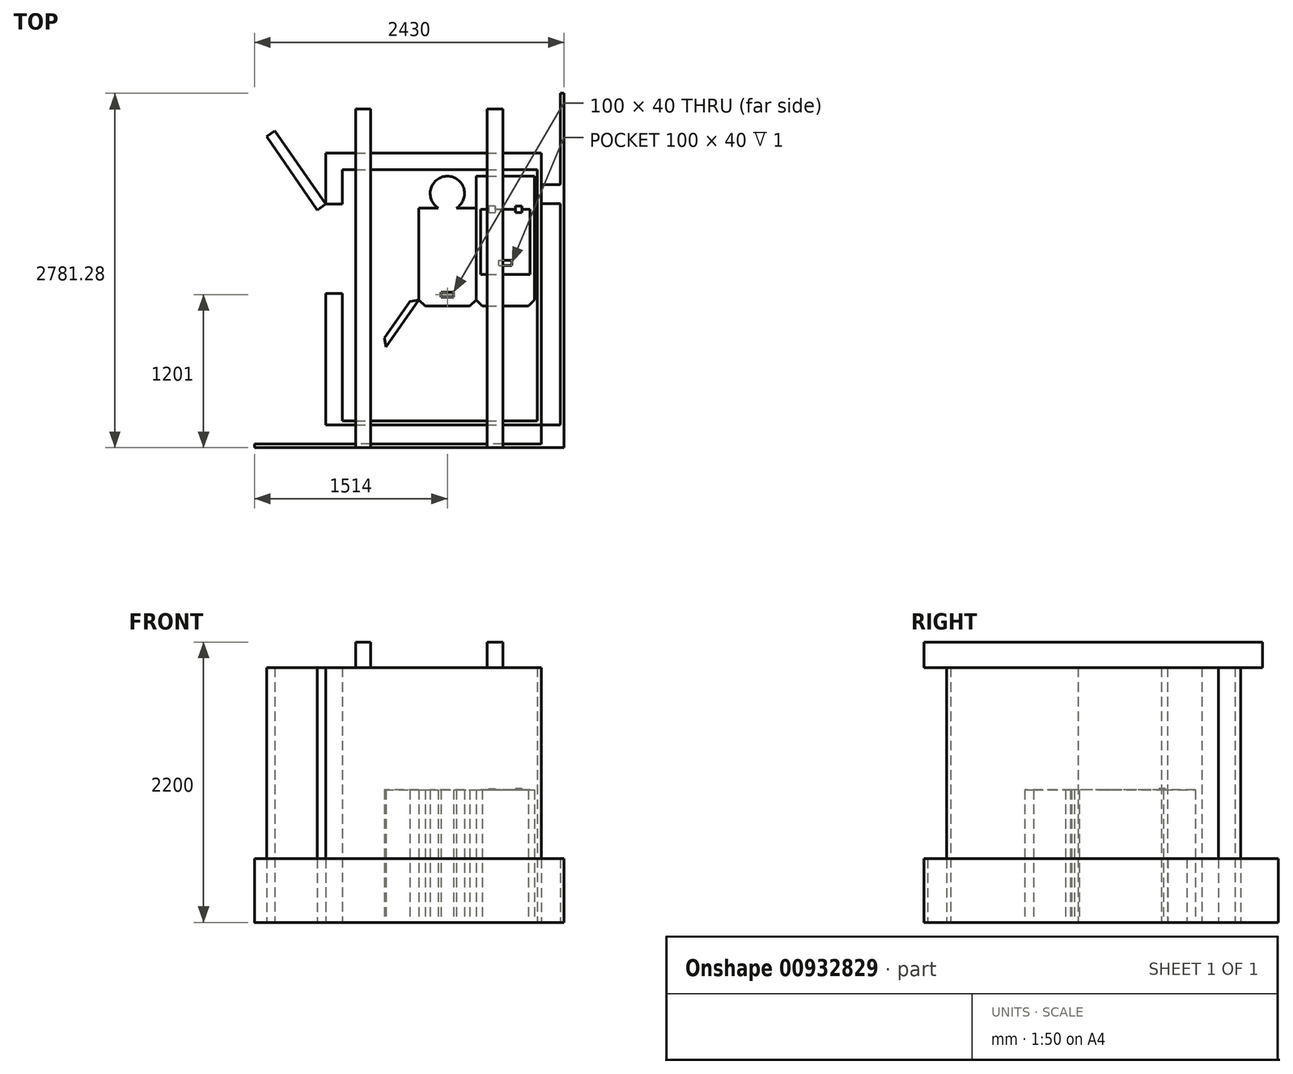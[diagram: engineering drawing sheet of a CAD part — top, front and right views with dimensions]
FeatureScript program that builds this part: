
annotation { "Feature Type Name" : "Feature", "Feature Type Description" : "" }
export const myFeature = defineFeature(function(context is Context, id is Id, definition is map)
    precondition{}
    {
        {
            var Q0;
            Q0=qCreatedBy(makeId("Top.planeOp"),FACE);
            var sketch = newSketch(context, id + "F0", { "sketchPlane" : qUnion([Q0])});
            skLineSegment(sketch, "E0", {"start": v(-30, 2781.28) * mm, "end": v(-30, 30) * mm});
            skLineSegment(sketch, "E1", {"start": v(-30, 30) * mm, "end": v(-2430, 30) * mm});
            skLineSegment(sketch, "E2", {"start": v(-2430, 30) * mm, "end": v(-2430, 0) * mm});
            skLineSegment(sketch, "E3", {"start": v(-2430, 0) * mm, "end": v(0, 0) * mm});
            skLineSegment(sketch, "E4", {"start": v(0, 0) * mm, "end": v(0, 2781.28) * mm});
            skLineSegment(sketch, "E5", {"start": v(0, 2781.28) * mm, "end": v(-30, 2781.28) * mm});
            skLineSegment(sketch, "E6", {"start": v(-2460, -1250) * mm, "end": v(-2460, 0) * mm});
            skLineSegment(sketch, "E7", {"start": v(-2460, 0) * mm, "end": v(-2430, 0) * mm});
            skLineSegment(sketch, "E8", {"start": v(-2430, 0) * mm, "end": v(-2430, -1250) * mm});
            skLineSegment(sketch, "E9", {"start": v(-2430, -1250) * mm, "end": v(-2460, -1250) * mm});
            skArc(sketch, "E10", {"start": v(-2460, -1250) * mm, "mid": v(-3343.88, -883.88) * mm, "end": v(-3710, 0) * mm, "construction": true});
            skLineSegment(sketch, "E11.bottom", {"start": v(-1872, 180) * mm, "end": v(-180, 180) * mm});
            skLineSegment(sketch, "E11.top", {"start": v(-1872, 2312) * mm, "end": v(-180, 2312) * mm});
            skLineSegment(sketch, "E11.right", {"start": v(-180, 180) * mm, "end": v(-180, 2312) * mm});
            skLineSegment(sketch, "E12.bottom", {"start": v(-1741, 2181) * mm, "end": v(-211, 2181) * mm});
            skLineSegment(sketch, "E12.top", {"start": v(-1741, 211) * mm, "end": v(-211, 211) * mm});
            skLineSegment(sketch, "E12.left", {"start": v(-1741, 2181) * mm, "end": v(-1741, 1911) * mm});
            skLineSegment(sketch, "E12.right", {"start": v(-211, 2181) * mm, "end": v(-211, 211) * mm});
            skLineSegment(sketch, "E13", {"start": v(-1872, 1911) * mm, "end": v(-1741, 1911) * mm});
            skLineSegment(sketch, "E14.trimOffspring", {"start": v(-1872, 1911) * mm, "end": v(-1872, 2312) * mm});
            skLineSegment(sketch, "E15", {"start": v(-211, 2312) * mm, "end": v(-211, 2181) * mm});
            skLineSegment(sketch, "E16", {"start": v(-180, 2181) * mm, "end": v(-211, 2181) * mm});
            skLineSegment(sketch, "E17", {"start": v(-180, 211) * mm, "end": v(-211, 211) * mm});
            skLineSegment(sketch, "E18", {"start": v(-211, 180) * mm, "end": v(-211, 211) * mm});
            skLineSegment(sketch, "E19", {"start": v(-1741, 211) * mm, "end": v(-1741, 1211) * mm});
            skLineSegment(sketch, "E20", {"start": v(-1741, 1211) * mm, "end": v(-1872, 1211) * mm});
            skLineSegment(sketch, "E21", {"start": v(-1872, 1211) * mm, "end": v(-1872, 180) * mm});
            skLineSegment(sketch, "E22.bottom", {"start": v(-1141, 1881) * mm, "end": v(-691, 1881) * mm});
            skLineSegment(sketch, "E22.top", {"start": v(-1091, 1111) * mm, "end": v(-741, 1111) * mm});
            skLineSegment(sketch, "E22.left", {"start": v(-1141, 1881) * mm, "end": v(-1141, 1161) * mm});
            skLineSegment(sketch, "E22.right", {"start": v(-231, 2131) * mm, "end": v(-231, 1161) * mm});
            skLineSegment(sketch, "E23.bottom", {"start": v(-2430, 30) * mm, "end": v(-2280, 30) * mm});
            skLineSegment(sketch, "E23.top", {"start": v(-2430, 180) * mm, "end": v(-2280, 180) * mm});
            skLineSegment(sketch, "E23.left", {"start": v(-2430, 30) * mm, "end": v(-2430, 180) * mm});
            skLineSegment(sketch, "E23.right", {"start": v(-2280, 30) * mm, "end": v(-2280, 180) * mm});
            skLineSegment(sketch, "E24.bottom", {"start": v(-180, 180) * mm, "end": v(-30, 180) * mm});
            skLineSegment(sketch, "E24.top", {"start": v(-180, 30) * mm, "end": v(-30, 30) * mm});
            skLineSegment(sketch, "E24.left", {"start": v(-180, 180) * mm, "end": v(-180, 30) * mm});
            skLineSegment(sketch, "E24.right", {"start": v(-30, 180) * mm, "end": v(-30, 30) * mm});
            skLineSegment(sketch, "E25.bottom", {"start": v(-180, 2065.03) * mm, "end": v(-30, 2065.03) * mm});
            skLineSegment(sketch, "E25.top", {"start": v(-180, 1915.03) * mm, "end": v(-30, 1915.03) * mm});
            skLineSegment(sketch, "E25.left", {"start": v(-180, 2065.03) * mm, "end": v(-180, 1915.03) * mm});
            skLineSegment(sketch, "E25.right", {"start": v(-30, 2065.03) * mm, "end": v(-30, 1915.03) * mm});
            skLineSegment(sketch, "E26.bottom", {"start": v(-1872, 1911) * mm, "end": v(-2269.59, 2487.13) * mm});
            skLineSegment(sketch, "E26.left", {"start": v(-2269.59, 2487.13) * mm, "end": v(-2335.43, 2441.69) * mm});
            skLineSegment(sketch, "E26.right", {"start": v(-1872, 1911) * mm, "end": v(-1937.84, 1865.56) * mm});
            skLineSegment(sketch, "E27", {"start": v(-1937.84, 1865.56) * mm, "end": v(-2335.43, 2441.69) * mm});
            skLineSegment(sketch, "E28.bottom", {"start": v(-4960, 0) * mm, "end": v(-4930, 0) * mm});
            skLineSegment(sketch, "E28.top", {"start": v(-4960, -1250) * mm, "end": v(-4930, -1250) * mm});
            skLineSegment(sketch, "E28.left", {"start": v(-4960, 0) * mm, "end": v(-4960, -1250) * mm});
            skLineSegment(sketch, "E28.right", {"start": v(-4930, 0) * mm, "end": v(-4930, -1250) * mm});
            skArc(sketch, "E29", {"start": v(-4960, -1250) * mm, "mid": v(-4076.12, -883.88) * mm, "end": v(-3710, 0) * mm, "construction": true});
            skLineSegment(sketch, "E30", {"start": v(-691, 1881) * mm, "end": v(-691, 1161) * mm});
            skLineSegment(sketch, "E31", {"start": v(-1141, 1161) * mm, "end": v(-1091, 1111) * mm});
            skLineSegment(sketch, "E32", {"start": v(-741, 1111) * mm, "end": v(-691, 1161) * mm});
            skLineSegment(sketch, "E33", {"start": v(-691, 1161) * mm, "end": v(-641, 1111) * mm});
            skLineSegment(sketch, "E34", {"start": v(-281, 1111) * mm, "end": v(-231, 1161) * mm});
            skLineSegment(sketch, "E35", {"start": v(-1141, 1161) * mm, "end": v(-1399.24, 792.47) * mm});
            skLineSegment(sketch, "E36", {"start": v(-1399.24, 792.47) * mm, "end": v(-1411.5, 862.11) * mm});
            skLineSegment(sketch, "E37", {"start": v(-1411.5, 862.11) * mm, "end": v(-1210.64, 1148.75) * mm});
            skLineSegment(sketch, "E38", {"start": v(-1210.64, 1148.75) * mm, "end": v(-1141, 1161) * mm});
            skLineSegment(sketch, "E39.trimOffspring", {"start": v(-641, 1111) * mm, "end": v(-281, 1111) * mm});
            skLineSegment(sketch, "E40", {"start": v(-691, 1881) * mm, "end": v(-691, 2131) * mm});
            skLineSegment(sketch, "E41", {"start": v(-691, 2131) * mm, "end": v(-231, 2131) * mm});
            skLineSegment(sketch, "E42.bottom", {"start": v(-966, 1221) * mm, "end": v(-866, 1221) * mm});
            skLineSegment(sketch, "E42.top", {"start": v(-966, 1181) * mm, "end": v(-866, 1181) * mm});
            skLineSegment(sketch, "E42.left", {"start": v(-966, 1221) * mm, "end": v(-966, 1181) * mm});
            skLineSegment(sketch, "E42.right", {"start": v(-866, 1221) * mm, "end": v(-866, 1181) * mm});
            skCircle(sketch, "E43", {"center": v(-1141, 1161) * mm, "radius": 0.5 * mm});
            skCircle(sketch, "E44", {"center": v(-2430, 0) * mm, "radius": 0.5 * mm});
            skLineSegment(sketch, "E45", {"start": v(-966, 1201) * mm, "end": v(-1141, 1201) * mm, "construction": true});
            skLineSegment(sketch, "E46", {"start": v(-866, 1201) * mm, "end": v(-691, 1201) * mm, "construction": true});
            skLineSegment(sketch, "E47.bottom", {"start": v(-656, 1871) * mm, "end": v(-266, 1871) * mm});
            skLineSegment(sketch, "E47.top", {"start": v(-656, 1361) * mm, "end": v(-266, 1361) * mm});
            skLineSegment(sketch, "E47.left", {"start": v(-656, 1871) * mm, "end": v(-656, 1361) * mm});
            skLineSegment(sketch, "E47.right", {"start": v(-266, 1871) * mm, "end": v(-266, 1361) * mm});
            skLineSegment(sketch, "E48", {"start": v(-656, 1616) * mm, "end": v(-691, 1616) * mm, "construction": true});
            skLineSegment(sketch, "E49", {"start": v(-266, 1616) * mm, "end": v(-231, 1616) * mm, "construction": true});
            skLineSegment(sketch, "E50.bottom", {"start": v(-591, 1896) * mm, "end": v(-541, 1896) * mm});
            skLineSegment(sketch, "E50.top", {"start": v(-591, 1846) * mm, "end": v(-541, 1846) * mm});
            skLineSegment(sketch, "E50.left", {"start": v(-591, 1896) * mm, "end": v(-591, 1846) * mm});
            skLineSegment(sketch, "E50.right", {"start": v(-541, 1896) * mm, "end": v(-541, 1846) * mm});
            skLineSegment(sketch, "E51", {"start": v(-461, 1871) * mm, "end": v(-461, 1361) * mm, "construction": true});
            skLineSegment(sketch, "E52.MirrorCS", {"start": v(-381, 1896) * mm, "end": v(-381, 1846) * mm});
            skLineSegment(sketch, "E53.MirrorCS", {"start": v(-331, 1896) * mm, "end": v(-331, 1846) * mm});
            skLineSegment(sketch, "E54.MirrorCS", {"start": v(-331, 1846) * mm, "end": v(-381, 1846) * mm});
            skLineSegment(sketch, "E55.MirrorCS", {"start": v(-331, 1896) * mm, "end": v(-381, 1896) * mm});
            skLineSegment(sketch, "E56.bottom", {"start": v(-511, 1471) * mm, "end": v(-411, 1471) * mm});
            skLineSegment(sketch, "E56.top", {"start": v(-511, 1431) * mm, "end": v(-411, 1431) * mm});
            skLineSegment(sketch, "E56.left", {"start": v(-511, 1471) * mm, "end": v(-511, 1431) * mm});
            skLineSegment(sketch, "E56.right", {"start": v(-411, 1471) * mm, "end": v(-411, 1431) * mm});
            skArc(sketch, "E57", {"start": v(-2269.59, 2487.13) * mm, "mid": v(-2540.31, 1702.78) * mm, "end": v(-1872, 1211) * mm, "construction": true});
            skCircle(sketch, "E58", {"center": v(-1872, 1911) * mm, "radius": 0.45 * mm});
            skLineSegment(sketch, "E59.bottom", {"start": v(-981, 1946.09) * mm, "end": v(-851, 1946.09) * mm});
            skLineSegment(sketch, "E59.top", {"start": v(-981, 1881) * mm, "end": v(-851, 1881) * mm});
            skLineSegment(sketch, "E59.left", {"start": v(-981, 1946.09) * mm, "end": v(-981, 1881) * mm});
            skLineSegment(sketch, "E59.right", {"start": v(-851, 1946.09) * mm, "end": v(-851, 1881) * mm});
            skLineSegment(sketch, "E60", {"start": v(-916, 1881) * mm, "end": v(-916, 1651.54) * mm, "construction": true});
            skCircle(sketch, "E61", {"center": v(-916, 1996) * mm, "radius": 135 * mm});
            skCircle(sketch, "E62", {"center": v(-916, 1996) * mm, "radius": 185 * mm, "construction": true});
            skSolve(sketch);
        }
        {
            var Q0;
            Q0=makeQuery(id+"F0.imprint","IMPRINT",FACE,{"disambiguationData":[TD([[makeQuery(id+"F0.imprint","IMPRINT",EDGE,{"derivedFrom":sQuery(id+"F0.wireOp",EDGE,"E22.bottom")}),-1.0]])]});
            var Q1;
            Q1=makeQuery(id+"F0.imprint","IMPRINT",FACE,{"disambiguationData":[TD([[makeQuery(id+"F0.imprint","IMPRINT",EDGE,{"derivedFrom":sQuery(id+"F0.wireOp",EDGE,"E35")}),-1.0]])]});
            var Q2;
            {var subQ6=sQuery(id+"F0.wireOp",EDGE,"E36");Q2=makeQuery(id+"F0.imprint","IMPRINT",FACE,{"disambiguationData":[TD([[makeQuery(id+"F0.imprint","IMPRINT",EDGE,{"derivedFrom":subQ6}),-1.0]])]});}
            var Q3;
            {var subQ1=sQuery(id+"F0.wireOp",EDGE,"E22.left");var subQ3=sQuery(id+"F0.wireOp",EDGE,"E43");var subQ4=makeQuery(id+"F0.imprint","INTERSECT",VERTEX,{"derivedFrom":[subQ1,subQ3]});Q3=makeQuery(id+"F0.imprint","IMPRINT",FACE,{"disambiguationData":[TD([[makeQuery(id+"F0.imprint","IMPRINT",EDGE,{"disambiguationData":[TD([[subQ4,1.0]])],"derivedFrom":subQ3}),1.0]])]});}
            var Q4;
            {var subQ1=sQuery(id+"F0.wireOp",EDGE,"E31");var subQ3=sQuery(id+"F0.wireOp",EDGE,"E43");var subQ4=makeQuery(id+"F0.imprint","INTERSECT",VERTEX,{"derivedFrom":[subQ1,subQ3]});Q4=makeQuery(id+"F0.imprint","IMPRINT",FACE,{"disambiguationData":[TD([[makeQuery(id+"F0.imprint","IMPRINT",EDGE,{"disambiguationData":[TD([[subQ4,1.0]])],"derivedFrom":subQ3}),1.0]])]});}
            var Q5;
            {var subQ1=sQuery(id+"F0.wireOp",EDGE,"E22.left");var subQ3=sQuery(id+"F0.wireOp",EDGE,"E43");var subQ4=makeQuery(id+"F0.imprint","INTERSECT",VERTEX,{"derivedFrom":[subQ1,subQ3]});Q5=makeQuery(id+"F0.imprint","IMPRINT",FACE,{"disambiguationData":[TD([[makeQuery(id+"F0.imprint","IMPRINT",EDGE,{"disambiguationData":[TD([[subQ4,-1.0]])],"derivedFrom":subQ3}),1.0]])]});}
            var Q6;
            {var subQ6=sQuery(id+"F0.wireOp",EDGE,"E22.top");Q6=makeQuery(id+"F0.imprint","IMPRINT",FACE,{"disambiguationData":[TD([[makeQuery(id+"F0.imprint","IMPRINT",EDGE,{"derivedFrom":subQ6}),1.0]])]});}
            var Q7;
            Q7=makeQuery(id+"F0.imprint","IMPRINT",FACE,{"disambiguationData":[TD([[makeQuery(id+"F0.imprint","IMPRINT",EDGE,{"derivedFrom":sQuery(id+"F0.wireOp",EDGE,"E59.bottom")}),-1.0]])]});
            var Q8;
            Q8=makeQuery(id+"F0.imprint","IMPRINT",FACE,{"disambiguationData":[TD([[makeQuery(id+"F0.imprint","IMPRINT",EDGE,{"derivedFrom":sQuery(id+"F0.wireOp",EDGE,"E59.bottom")}),1.0]])]});
            extrude(context, id + "F1", {"entities" : qUnion([Q0, Q1, Q2, Q3, Q4, Q5, Q6, Q7, Q8]), "depth" : 1040 * mm, "offsetDistance" : 25 * mm});
        }
        {
            var Q0;
            Q0=makeQuery(id+"F0.imprint","IMPRINT",FACE,{"disambiguationData":[TD([[makeQuery(id+"F0.imprint","IMPRINT",EDGE,{"derivedFrom":sQuery(id+"F0.wireOp",EDGE,"E22.right")}),-1.0]])]});
            var Q1;
            Q1=makeQuery(id+"F0.imprint","IMPRINT",FACE,{"disambiguationData":[TD([[makeQuery(id+"F0.imprint","IMPRINT",EDGE,{"derivedFrom":sQuery(id+"F0.wireOp",EDGE,"b8486e81-6a5e-4ac8-b1f6-dfdbe80d117f0.MirrorCS")}),1.0]])]});
            var Q2;
            Q2=makeQuery(id+"F0.imprint","IMPRINT",FACE,{"disambiguationData":[TD([[makeQuery(id+"F0.imprint","IMPRINT",EDGE,{"derivedFrom":sQuery(id+"F0.wireOp",EDGE,"688ad7da-94cf-4359-b2d6-07f1512130790.MirrorCS")}),1.0]])]});
            var Q3;
            Q3=makeQuery(id+"F0.imprint","IMPRINT",FACE,{"disambiguationData":[TD([[makeQuery(id+"F0.imprint","IMPRINT",EDGE,{"derivedFrom":sQuery(id+"F0.wireOp",EDGE,"E56.bottom")}),-1.0]])]});
            var Q4;
            Q4=makeQuery(id+"F0.imprint","IMPRINT",FACE,{"disambiguationData":[TD([[makeQuery(id+"F0.imprint","IMPRINT",EDGE,{"derivedFrom":sQuery(id+"F0.wireOp",EDGE,"E47.top")}),1.0]])]});
            var Q5;
            {var subQ5=sQuery(id+"F0.wireOp",EDGE,"E50.top");Q5=makeQuery(id+"F0.imprint","IMPRINT",FACE,{"disambiguationData":[TD([[makeQuery(id+"F0.imprint","IMPRINT",EDGE,{"derivedFrom":subQ5}),1.0]])]});}
            var Q6;
            {var subQ5=sQuery(id+"F0.wireOp",EDGE,"E50.bottom");Q6=makeQuery(id+"F0.imprint","IMPRINT",FACE,{"disambiguationData":[TD([[makeQuery(id+"F0.imprint","IMPRINT",EDGE,{"derivedFrom":subQ5}),-1.0]])]});}
            var Q7;
            {var subQ5=sQuery(id+"F0.wireOp",EDGE,"E55.MirrorCS");Q7=makeQuery(id+"F0.imprint","IMPRINT",FACE,{"disambiguationData":[TD([[makeQuery(id+"F0.imprint","IMPRINT",EDGE,{"derivedFrom":subQ5}),1.0]])]});}
            var Q8;
            {var subQ5=sQuery(id+"F0.wireOp",EDGE,"E54.MirrorCS");Q8=makeQuery(id+"F0.imprint","IMPRINT",FACE,{"disambiguationData":[TD([[makeQuery(id+"F0.imprint","IMPRINT",EDGE,{"derivedFrom":subQ5}),-1.0]])]});}
            extrude(context, id + "F2", {"entities" : qUnion([Q0, Q1, Q2, Q3, Q4, Q5, Q6, Q7, Q8]), "depth" : 1040 * mm, "offsetDistance" : 25 * mm});
        }
        {
            var Q0;
            Q0=makeQuery(id+"F0.imprint","IMPRINT",FACE,{"disambiguationData":[TD([[makeQuery(id+"F0.imprint","IMPRINT",EDGE,{"derivedFrom":sQuery(id+"F0.wireOp",EDGE,"E47.top")}),1.0]])]});
            extrude(context, id + "F3", {"entities" : qUnion([Q0]), "operationType" : NewBodyOperationType.ADD, "depth" : 1041 * mm, "offsetDistance" : 25 * mm});
        }
        {
            var Q0;
            {var subQ5=sQuery(id+"F0.wireOp",EDGE,"E50.bottom");Q0=makeQuery(id+"F0.imprint","IMPRINT",FACE,{"disambiguationData":[TD([[makeQuery(id+"F0.imprint","IMPRINT",EDGE,{"derivedFrom":subQ5}),-1.0]])]});}
            var Q1;
            {var subQ5=sQuery(id+"F0.wireOp",EDGE,"E50.top");Q1=makeQuery(id+"F0.imprint","IMPRINT",FACE,{"disambiguationData":[TD([[makeQuery(id+"F0.imprint","IMPRINT",EDGE,{"derivedFrom":subQ5}),1.0]])]});}
            var Q2;
            {var subQ5=sQuery(id+"F0.wireOp",EDGE,"E55.MirrorCS");Q2=makeQuery(id+"F0.imprint","IMPRINT",FACE,{"disambiguationData":[TD([[makeQuery(id+"F0.imprint","IMPRINT",EDGE,{"derivedFrom":subQ5}),1.0]])]});}
            var Q3;
            {var subQ5=sQuery(id+"F0.wireOp",EDGE,"E54.MirrorCS");Q3=makeQuery(id+"F0.imprint","IMPRINT",FACE,{"disambiguationData":[TD([[makeQuery(id+"F0.imprint","IMPRINT",EDGE,{"derivedFrom":subQ5}),-1.0]])]});}
            extrude(context, id + "F4", {"entities" : qUnion([Q0, Q1, Q2, Q3]), "operationType" : NewBodyOperationType.ADD, "depth" : 1050 * mm, "offsetDistance" : 25 * mm});
        }
        {
            var Q0;
            Q0=makeQuery(id+"F0.imprint","IMPRINT",FACE,{"disambiguationData":[TD([[makeQuery(id+"F0.imprint","IMPRINT",EDGE,{"derivedFrom":sQuery(id+"F0.wireOp",EDGE,"E12.bottom")}),1.0]])]});
            var Q1;
            {var subQ3=sQuery(id+"F0.wireOp",EDGE,"E15");Q1=makeQuery(id+"F0.imprint","IMPRINT",FACE,{"disambiguationData":[TD([[makeQuery(id+"F0.imprint","IMPRINT",EDGE,{"derivedFrom":subQ3}),1.0]])]});}
            var Q2;
            Q2=makeQuery(id+"F0.imprint","IMPRINT",FACE,{"disambiguationData":[TD([[makeQuery(id+"F0.imprint","IMPRINT",EDGE,{"derivedFrom":sQuery(id+"F0.wireOp",EDGE,"E12.right")}),1.0]])]});
            var Q3;
            {var subQ4=sQuery(id+"F0.wireOp",EDGE,"E17");Q3=makeQuery(id+"F0.imprint","IMPRINT",FACE,{"disambiguationData":[TD([[makeQuery(id+"F0.imprint","IMPRINT",EDGE,{"derivedFrom":subQ4}),1.0]])]});}
            var Q4;
            Q4=makeQuery(id+"F0.imprint","IMPRINT",FACE,{"disambiguationData":[TD([[makeQuery(id+"F0.imprint","IMPRINT",EDGE,{"derivedFrom":sQuery(id+"F0.wireOp",EDGE,"E12.top")}),-1.0]])]});
            var Q5;
            Q5=makeQuery(id+"F0.imprint","IMPRINT",FACE,{"disambiguationData":[TD([[makeQuery(id+"F0.imprint","IMPRINT",EDGE,{"derivedFrom":sQuery(id+"F0.wireOp",EDGE,"E26.bottom")}),1.0]])]});
            var Q6;
            {var subQ1=sQuery(id+"F0.wireOp",EDGE,"E20");var subQ3=sQuery(id+"F0.wireOp",EDGE,"QImJkGrw-Z5Ot-RNPT-PDxS-a5AK5lmXrIYX");var subQ4=makeQuery(id+"F0.imprint","INTERSECT",VERTEX,{"derivedFrom":[subQ1,subQ3]});Q6=makeQuery(id+"F0.imprint","IMPRINT",FACE,{"disambiguationData":[TD([[makeQuery(id+"F0.imprint","IMPRINT",EDGE,{"disambiguationData":[TD([[subQ4,1.0]])],"derivedFrom":subQ3}),1.0]])]});}
            var Q7;
            {var subQ1=sQuery(id+"F0.wireOp",EDGE,"E19");var subQ3=sQuery(id+"F0.wireOp",EDGE,"QImJkGrw-Z5Ot-RNPT-PDxS-a5AK5lmXrIYX");var subQ4=makeQuery(id+"F0.imprint","INTERSECT",VERTEX,{"derivedFrom":[subQ1,subQ3]});Q7=makeQuery(id+"F0.imprint","IMPRINT",FACE,{"disambiguationData":[TD([[makeQuery(id+"F0.imprint","IMPRINT",EDGE,{"disambiguationData":[TD([[subQ4,1.0]])],"derivedFrom":subQ3}),1.0]])]});}
            var Q8;
            {var subQ1=sQuery(id+"F0.wireOp",EDGE,"E19");var subQ3=sQuery(id+"F0.wireOp",EDGE,"QImJkGrw-Z5Ot-RNPT-PDxS-a5AK5lmXrIYX");var subQ4=makeQuery(id+"F0.imprint","INTERSECT",VERTEX,{"derivedFrom":[subQ1,subQ3]});Q8=makeQuery(id+"F0.imprint","IMPRINT",FACE,{"disambiguationData":[TD([[makeQuery(id+"F0.imprint","IMPRINT",EDGE,{"disambiguationData":[TD([[subQ4,-1.0]])],"derivedFrom":subQ3}),1.0]])]});}
            var Q9;
            {var subQ1=sQuery(id+"F0.wireOp",EDGE,"E12.left");var subQ3=sQuery(id+"F0.wireOp",EDGE,"YpwpCyUx-jLYR-Vb0S-xmWT-aZwAgyBeGrC7");var subQ4=makeQuery(id+"F0.imprint","INTERSECT",VERTEX,{"derivedFrom":[subQ1,subQ3]});Q9=makeQuery(id+"F0.imprint","IMPRINT",FACE,{"disambiguationData":[TD([[makeQuery(id+"F0.imprint","IMPRINT",EDGE,{"disambiguationData":[TD([[subQ4,-1.0]])],"derivedFrom":subQ3}),1.0]])]});}
            var Q10;
            {var subQ1=sQuery(id+"F0.wireOp",EDGE,"E12.left");var subQ3=sQuery(id+"F0.wireOp",EDGE,"YpwpCyUx-jLYR-Vb0S-xmWT-aZwAgyBeGrC7");var subQ4=makeQuery(id+"F0.imprint","INTERSECT",VERTEX,{"derivedFrom":[subQ1,subQ3]});Q10=makeQuery(id+"F0.imprint","IMPRINT",FACE,{"disambiguationData":[TD([[makeQuery(id+"F0.imprint","IMPRINT",EDGE,{"disambiguationData":[TD([[subQ4,1.0]])],"derivedFrom":subQ3}),1.0]])]});}
            var Q11;
            {var subQ1=sQuery(id+"F0.wireOp",EDGE,"E26.right");var subQ3=sQuery(id+"F0.wireOp",EDGE,"YpwpCyUx-jLYR-Vb0S-xmWT-aZwAgyBeGrC7");var subQ4=makeQuery(id+"F0.imprint","INTERSECT",VERTEX,{"derivedFrom":[subQ1,subQ3]});Q11=makeQuery(id+"F0.imprint","IMPRINT",FACE,{"disambiguationData":[TD([[makeQuery(id+"F0.imprint","IMPRINT",EDGE,{"disambiguationData":[TD([[subQ4,-1.0]])],"derivedFrom":subQ3}),1.0]])]});}
            var Q12;
            {var subQ1=sQuery(id+"F0.wireOp",EDGE,"E13");var subQ3=sQuery(id+"F0.wireOp",EDGE,"E58");var subQ4=makeQuery(id+"F0.imprint","INTERSECT",VERTEX,{"derivedFrom":[subQ1,subQ3]});Q12=makeQuery(id+"F0.imprint","IMPRINT",FACE,{"disambiguationData":[TD([[makeQuery(id+"F0.imprint","IMPRINT",EDGE,{"disambiguationData":[TD([[subQ4,-1.0]])],"derivedFrom":subQ3}),1.0]])]});}
            var Q13;
            {var subQ1=sQuery(id+"F0.wireOp",EDGE,"E14.trimOffspring");var subQ3=sQuery(id+"F0.wireOp",EDGE,"E58");var subQ4=makeQuery(id+"F0.imprint","INTERSECT",VERTEX,{"derivedFrom":[subQ1,subQ3]});Q13=makeQuery(id+"F0.imprint","IMPRINT",FACE,{"disambiguationData":[TD([[makeQuery(id+"F0.imprint","IMPRINT",EDGE,{"disambiguationData":[TD([[subQ4,-1.0]])],"derivedFrom":subQ3}),1.0]])]});}
            var Q14;
            {var subQ4=sQuery(id+"F0.wireOp",EDGE,"E26.left");Q14=makeQuery(id+"F0.imprint","IMPRINT",FACE,{"disambiguationData":[TD([[makeQuery(id+"F0.imprint","IMPRINT",EDGE,{"derivedFrom":subQ4}),1.0]])]});}
            extrude(context, id + "F5", {"entities" : qUnion([Q0, Q1, Q2, Q3, Q4, Q5, Q6, Q7, Q8, Q9, Q10, Q11, Q12, Q13, Q14]), "depth" : 2000 * mm, "offsetDistance" : 25 * mm});
        }
        {
            var Q0;
            Q0=makeQuery(id+"F5.opExtrude","CAP_FACE",FACE,{"disambiguationData":[OSD([sQuery(id+"F0.wireOp",EDGE,"E11.bottom"),sQuery(id+"F0.wireOp",EDGE,"E11.top"),sQuery(id+"F0.wireOp",EDGE,"E11.right"),sQuery(id+"F0.wireOp",EDGE,"E12.bottom"),sQuery(id+"F0.wireOp",EDGE,"E12.top"),sQuery(id+"F0.wireOp",EDGE,"E12.left"),sQuery(id+"F0.wireOp",EDGE,"E12.right"),sQuery(id+"F0.wireOp",EDGE,"E13"),sQuery(id+"F0.wireOp",EDGE,"E14.trimOffspring"),sQuery(id+"F0.wireOp",EDGE,"E19"),sQuery(id+"F0.wireOp",EDGE,"E20"),sQuery(id+"F0.wireOp",EDGE,"E21"),sQuery(id+"F0.wireOp",EDGE,"E25.left"),sQuery(id+"F0.wireOp",EDGE,"E26.bottom"),sQuery(id+"F0.wireOp",EDGE,"E26.left"),sQuery(id+"F0.wireOp",EDGE,"E26.right"),sQuery(id+"F0.wireOp",EDGE,"E27"),sQuery(id+"F0.wireOp",EDGE,"YpwpCyUx-jLYR-Vb0S-xmWT-aZwAgyBeGrC7")])],"isStart":false});
            var sketch = newSketch(context, id + "F6", { "sketchPlane" : qUnion([Q0])});
            skLineSegment(sketch, "E63.bottom", {"start": v(-605, 2657.35) * mm, "end": v(-480, 2657.35) * mm});
            skLineSegment(sketch, "E63.top", {"start": v(-605, 0) * mm, "end": v(-480, 0) * mm});
            skLineSegment(sketch, "E63.left", {"start": v(-605, 2657.35) * mm, "end": v(-605, 0) * mm});
            skLineSegment(sketch, "E63.right", {"start": v(-480, 2657.35) * mm, "end": v(-480, 0) * mm});
            skLineSegment(sketch, "E64.bottom", {"start": v(-1635, 2657.35) * mm, "end": v(-1520, 2657.35) * mm});
            skLineSegment(sketch, "E64.top", {"start": v(-1635, 0) * mm, "end": v(-1520, 0) * mm});
            skLineSegment(sketch, "E64.left", {"start": v(-1635, 2657.35) * mm, "end": v(-1635, 0) * mm});
            skLineSegment(sketch, "E64.right", {"start": v(-1520, 2657.35) * mm, "end": v(-1520, 0) * mm});
            skSolve(sketch);
        }
        {
            var Q0;
            Q0 = qSketchRegion(id + "F6", true);
            extrude(context, id + "F7", {"entities" : qUnion([Q0]), "operationType" : NewBodyOperationType.ADD, "depth" : 200 * mm, "offsetDistance" : 25 * mm});
        }
        {
            var Q0;
            Q0=makeQuery(id+"F0.imprint","IMPRINT",FACE,{"disambiguationData":[TD([[makeQuery(id+"F0.imprint","IMPRINT",EDGE,{"derivedFrom":sQuery(id+"F0.wireOp",EDGE,"E23.bottom")}),1.0]])]});
            var Q1;
            Q1=makeQuery(id+"F0.imprint","IMPRINT",FACE,{"disambiguationData":[TD([[makeQuery(id+"F0.imprint","IMPRINT",EDGE,{"derivedFrom":sQuery(id+"F0.wireOp",EDGE,"E1")}),1.0]])]});
            var Q2;
            Q2=makeQuery(id+"F0.imprint","IMPRINT",FACE,{"disambiguationData":[TD([[makeQuery(id+"F0.imprint","IMPRINT",EDGE,{"derivedFrom":sQuery(id+"F0.wireOp",EDGE,"E24.bottom")}),-1.0]])]});
            var Q3;
            Q3=makeQuery(id+"F0.imprint","IMPRINT",FACE,{"disambiguationData":[TD([[makeQuery(id+"F0.imprint","IMPRINT",EDGE,{"derivedFrom":sQuery(id+"F0.wireOp",EDGE,"E25.bottom")}),-1.0]])]});
            extrude(context, id + "F8", {"entities" : qUnion([Q0, Q1, Q2, Q3]), "depth" : 500 * mm, "offsetDistance" : 25 * mm});
        }
    });
